# Revit family: FP_Revit_18_RF521TR_Fridges_90001134A
name_source: partatom
category: Specialty Equipment
revit_build: Autodesk Revit 2018 (Build: 20170223_1515(x64)
units: mm (PartAtom-declared; Revit-internal decimal feet)

## family parameters
Always vertical = Yes
Cut with Voids When Loaded = Yes
OmniClass Number = 23.40.40.11.11.17
OmniClass Title = Refrigerator-Freezer
Part Type = Normal
Room Calculation Point = No
Round Connector Dimension = Use Diameter
Shared = No
Work Plane-Based = No

## types (4) — shared parameters
Cavity - Depth = 625 mm  [stored 2.05052 ft]
Cavity - Height = 1735 mm  [stored 5.69226 ft]
Cavity - Width = 830 mm  [stored 2.7231 ft]
Chassis - Depth = 625 mm  [stored 2.05052 ft]
Chassis - Height = 1662 mm  [stored 5.45276 ft]
Chassis - Width = 790 mm  [stored 2.59186 ft]
Manufacturer = Fisher & Paykel Appliances
Material - Body = Fisher & Paykel - Grey
Material - Door Structure = Fisher & Paykel - White
Product - Depth = 695 mm  [stored 2.28018 ft]
Product - Height = 1720 mm
Product - Width = 790 mm  [stored 2.59186 ft]
URL = www.fisherpaykel.com
Visibility - Clearance Required = Yes

## per-type parameters (varying)
| type | Connector Description - Electrical | Description | Material - Door Front |
| RF521TRPX6 | 230 V, 10 A, fused electrical supply | 79cm Freestanding Refrigerator with Bottom Freezer (Stainless) | Fisher & Paykel - Stainless Steel |
| RF521TRZX6 | 230 V, 10 A, fused electrical supply | 79cm Freestanding Refrigerator with Bottom Freezer (Stainless) | Fisher & Paykel - Stainless Steel |
| RF521TRZW6 | 230 V, 10 A, fused electrical supply | 79cm Freestanding Refrigerator with Bottom Freezer (White) | Fisher & Paykel - White |
| RF521TRPW6 | 120 V, 10 A, fused electrical supply | 79cm Freestanding Refrigerator with Bottom Freezer (White) | Fisher & Paykel - White |

note: column(s) folded — value = type name in every type: Model

note: [stored X ft] marks values corroborated as IEEE doubles in the binary element streams (Revit-internal decimal feet)

## geometry (parser evidence)
native form markers: Sweep x5
no freeform markers — native parametric forms only
